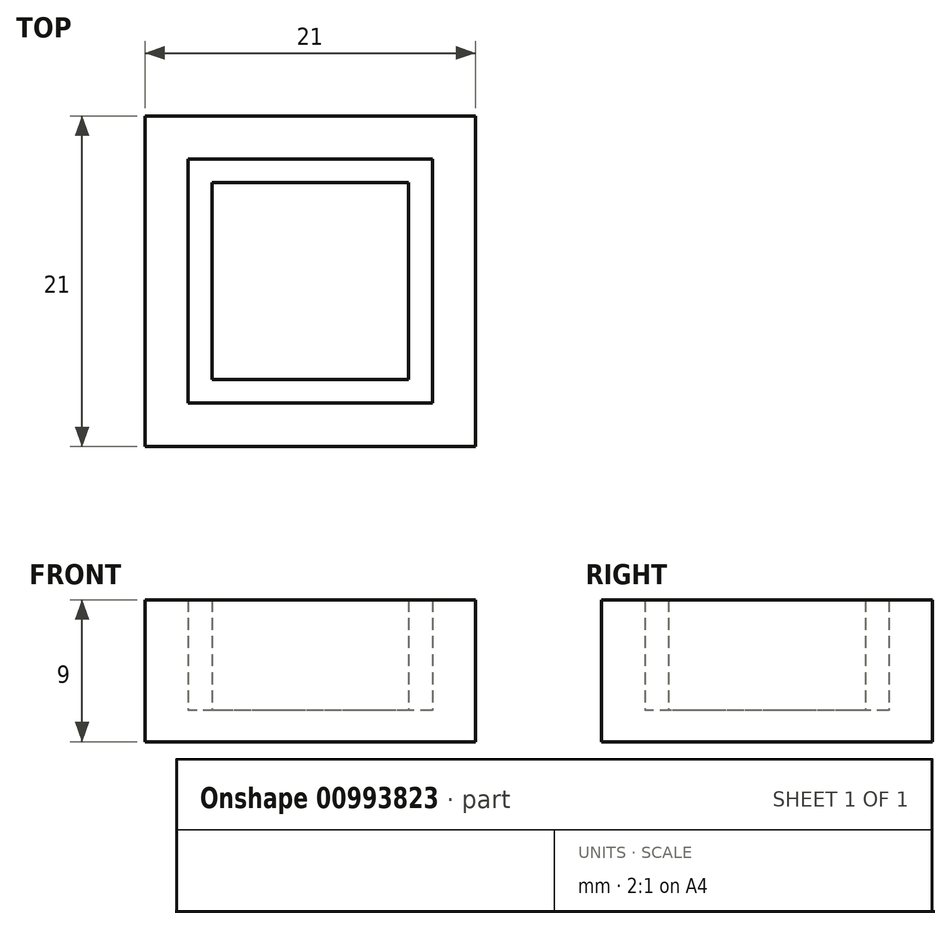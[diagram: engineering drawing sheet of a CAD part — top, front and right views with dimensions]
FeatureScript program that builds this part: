
annotation { "Feature Type Name" : "Feature", "Feature Type Description" : "" }
export const myFeature = defineFeature(function(context is Context, id is Id, definition is map)
    precondition{}
    {
        {
            var Q0;
            Q0=qCreatedBy(makeId("Top.planeOp"),FACE);
            var sketch = newSketch(context, id + "F0", { "sketchPlane" : qUnion([Q0])});
            skLineSegment(sketch, "E0.bottom", {"start": v(10.5, 10.5) * mm, "end": v(-10.5, 10.5) * mm});
            skLineSegment(sketch, "E0.top", {"start": v(10.5, -10.5) * mm, "end": v(-10.5, -10.5) * mm});
            skLineSegment(sketch, "E0.left", {"start": v(10.5, 10.5) * mm, "end": v(10.5, -10.5) * mm});
            skLineSegment(sketch, "E0.right", {"start": v(-10.5, 10.5) * mm, "end": v(-10.5, -10.5) * mm});
            skPoint(sketch, "E0.middle", {"position": v(0, 0) * mm});
            skLineSegment(sketch, "E1.bottom", {"start": v(7.75, 7.75) * mm, "end": v(-7.75, 7.75) * mm});
            skLineSegment(sketch, "E1.top", {"start": v(7.75, -7.75) * mm, "end": v(-7.75, -7.75) * mm});
            skLineSegment(sketch, "E1.left", {"start": v(7.75, 7.75) * mm, "end": v(7.75, -7.75) * mm});
            skLineSegment(sketch, "E1.right", {"start": v(-7.75, 7.75) * mm, "end": v(-7.75, -7.75) * mm});
            skLineSegment(sketch, "E2.0", {"start": v(6.25, 6.25) * mm, "end": v(-6.25, 6.25) * mm});
            skLineSegment(sketch, "E2.1", {"start": v(6.25, 6.25) * mm, "end": v(6.25, -6.25) * mm});
            skLineSegment(sketch, "E2.2", {"start": v(6.25, -6.25) * mm, "end": v(-6.25, -6.25) * mm});
            skLineSegment(sketch, "E2.3", {"start": v(-6.25, 6.25) * mm, "end": v(-6.25, -6.25) * mm});
            skSolve(sketch);
        }
        {
            var Q0;
            Q0 = qSketchRegion(id + "F0", true);
            var Q1;
            Q1=makeQuery(id+"F0.imprint","IMPRINT",FACE,{"disambiguationData":[TD([[makeQuery(id+"F0.imprint","IMPRINT",EDGE,{"derivedFrom":sQuery(id+"F0.wireOp",EDGE,"E1.bottom")}),1.0]])]});
            var Q2;
            Q2=makeQuery(id+"F0.imprint","IMPRINT",FACE,{"disambiguationData":[TD([[makeQuery(id+"F0.imprint","IMPRINT",EDGE,{"derivedFrom":sQuery(id+"F0.wireOp",EDGE,"E2.0")}),1.0]])]});
            extrude(context, id + "F1", {"entities" : qUnion([Q0, Q1, Q2]), "oppositeDirection" : true, "depth" : 2 * mm, "offsetDistance" : 25 * mm});
        }
        {
            var Q0;
            Q0=makeQuery(id+"F0.imprint","IMPRINT",FACE,{"disambiguationData":[TD([[makeQuery(id+"F0.imprint","IMPRINT",EDGE,{"derivedFrom":sQuery(id+"F0.wireOp",EDGE,"E0.bottom")}),1.0]])]});
            var Q1;
            Q1=makeQuery(id+"F0.imprint","IMPRINT",FACE,{"disambiguationData":[TD([[makeQuery(id+"F0.imprint","IMPRINT",EDGE,{"derivedFrom":sQuery(id+"F0.wireOp",EDGE,"E2.0")}),1.0]])]});
            extrude(context, id + "F2", {"entities" : qUnion([Q0, Q1]), "operationType" : NewBodyOperationType.ADD, "depth" : 7 * mm, "offsetDistance" : 25 * mm});
        }
    });
